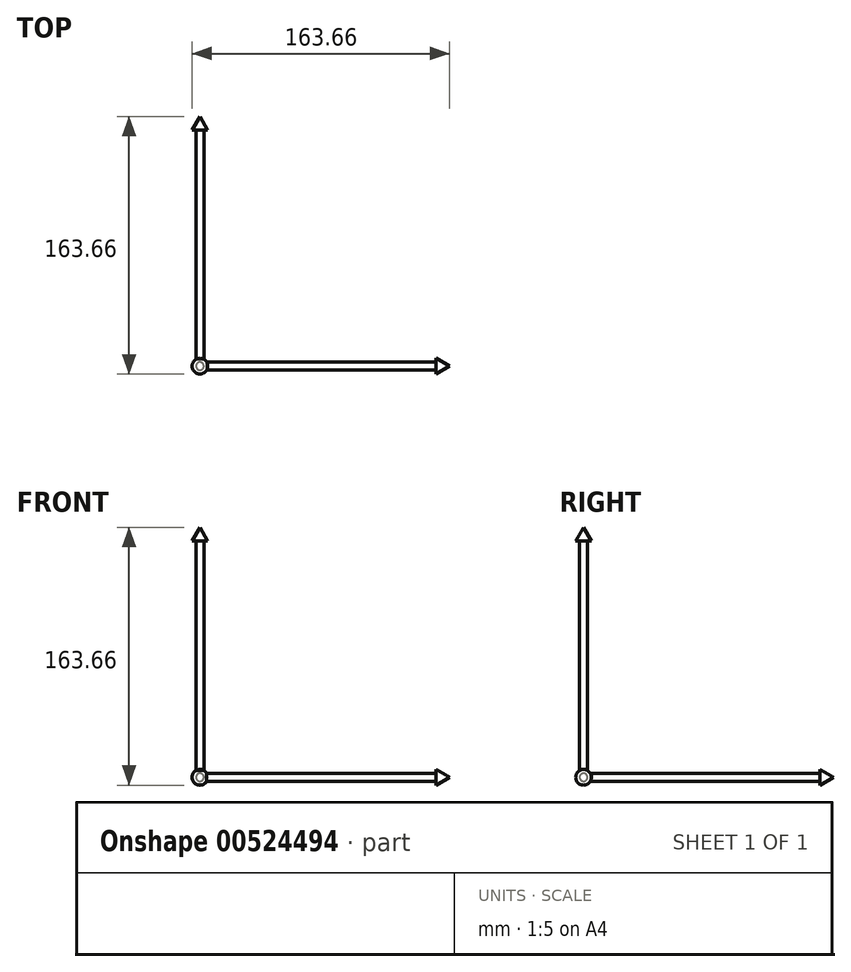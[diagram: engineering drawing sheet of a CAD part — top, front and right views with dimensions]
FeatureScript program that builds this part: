
annotation { "Feature Type Name" : "Feature", "Feature Type Description" : "" }
export const myFeature = defineFeature(function(context is Context, id is Id, definition is map)
    precondition{}
    {
        {
            assignVariable(context, id + "F0", {"name" : "lengthY", "anyValue" : 150});
        }
        {
            var Q0;
            Q0=qCreatedBy(makeId("Front.planeOp"),FACE);
            var sketch = newSketch(context, id + "F1", { "sketchPlane" : qUnion([Q0])});
            skArc(sketch, "E0", {"start": v(-5, 0) * mm, "mid": v(0, 5) * mm, "end": v(5, 0) * mm});
            skLineSegment(sketch, "E1", {"start": v(5, 0) * mm, "end": v(-5, 0) * mm});
            skSolve(sketch);
        }
        {
            var Q0;
            Q0=qSketchRegion(id+"F1",true);
            var Q1;
            Q1=sQuery(id+"F1.wireOp",EDGE,"E1");
            revolve(context, id + "F2", {"entities" : qUnion([Q0]), "axis" : qUnion([Q1]), "revolveType" : RevolveType.FULL});
        }
        {
            var Q0;
            Q0=qCreatedBy(makeId("Front.planeOp"),FACE);
            var sketch = newSketch(context, id + "F3", { "sketchPlane" : qUnion([Q0])});
            skCircle(sketch, "E2", {"center": v(0, 0) * mm, "radius": 2.5 * mm});
            skSolve(sketch);
        }
        {
            var Q0;
            Q0=qSketchRegion(id+"F3",true);
            extrude(context, id + "F4", {"entities" : qUnion([Q0]), "operationType" : NewBodyOperationType.ADD, "oppositeDirection" : true, "depth" : (getVariable(context, 'lengthY')) * mm, "offsetDistance" : 25 * mm});
        }
        {
            var Q0;
            Q0=makeQuery(id+"F4.opExtrude","CAP_FACE",FACE,{"disambiguationData":[OSD([sQuery(id+"F3.wireOp",EDGE,"E2")])],"isStart":false});
            var sketch = newSketch(context, id + "F5", { "sketchPlane" : qUnion([Q0])});
            skCircle(sketch, "E3", {"center": v(0, 0) * mm, "radius": 5 * mm});
            skSolve(sketch);
        }
        {
            var Q0;
            Q0=qSketchRegion(id+"F5",true);
            extrude(context, id + "F6", {"entities" : qUnion([Q0]), "operationType" : NewBodyOperationType.ADD, "depth" : 25 * mm, "offsetDistance" : 25 * mm, "hasDraft" : true, "draftAngle" : 30 * degree, "draftPullDirection" : true});
        }
        {
            var Q0;
            Q0=qCreatedBy(makeId("Front.planeOp"),FACE);
            var sketch = newSketch(context, id + "F7", { "sketchPlane" : qUnion([Q0])});
            skLineSegment(sketch, "E4", {"start": v(0, 13.06) * mm, "end": v(0, 0) * mm});
            skLineSegment(sketch, "E5", {"start": v(0, 0) * mm, "end": v(17.73, 0) * mm});
            skSolve(sketch);
        }
        {
            var Q0;
            Q0=makeQuery(id+"F2.opRevolve","SWEPT_BODY",BODY,{"disambiguationData":[OSD([sQuery(id+"F1.wireOp",EDGE,"E0"),sQuery(id+"F1.wireOp",EDGE,"E1")])]});
            var Q1;
            Q1=sQuery(id+"F7.wireOp",EDGE,"E4");
            circularPattern(context, id + "F8", {"entities" : qUnion([Q0]), "axis" : qUnion([Q1]), "angle" : 90 * degree, "instanceCount" : 2, "equalSpace" : true});
        }
        {
            var Q0;
            Q0=makeQuery(id+"F2.opRevolve","SWEPT_BODY",BODY,{"disambiguationData":[OSD([sQuery(id+"F1.wireOp",EDGE,"E0"),sQuery(id+"F1.wireOp",EDGE,"E1")])]});
            var Q1;
            Q1=sQuery(id+"F7.wireOp",EDGE,"E5");
            circularPattern(context, id + "F9", {"entities" : qUnion([Q0]), "axis" : qUnion([Q1]), "angle" : 90 * degree, "instanceCount" : 2, "equalSpace" : true});
        }
        {
            var Q0;
            Q0=makeQuery(id+"F9.opPattern","COPY",BODY,{"derivedFrom":makeQuery(id+"F2.opRevolve","SWEPT_BODY",BODY,{"disambiguationData":[OSD([sQuery(id+"F1.wireOp",EDGE,"E0"),sQuery(id+"F1.wireOp",EDGE,"E1")])]}),"instanceName":"1"});
            transform(context, id + "F10", {"entities" : qUnion([Q0]), "transformType" : TransformType.TRANSLATION_3D, "dx" : 0 * mm, "dy" : 0 * mm, "dz" : 0 * mm, "makeCopy" : true});
        }
        {
            var Q0;
            Q0=makeQuery(id+"F10.opPattern","COPY",BODY,{"derivedFrom":makeQuery(id+"F9.opPattern","COPY",BODY,{"derivedFrom":makeQuery(id+"F2.opRevolve","SWEPT_BODY",BODY,{"disambiguationData":[OSD([sQuery(id+"F1.wireOp",EDGE,"E0"),sQuery(id+"F1.wireOp",EDGE,"E1")])]}),"instanceName":"1"}),"instanceName":"1"});
            deleteBodies(context, id + "F11", {"entities" : qUnion([Q0])});
        }
    });
